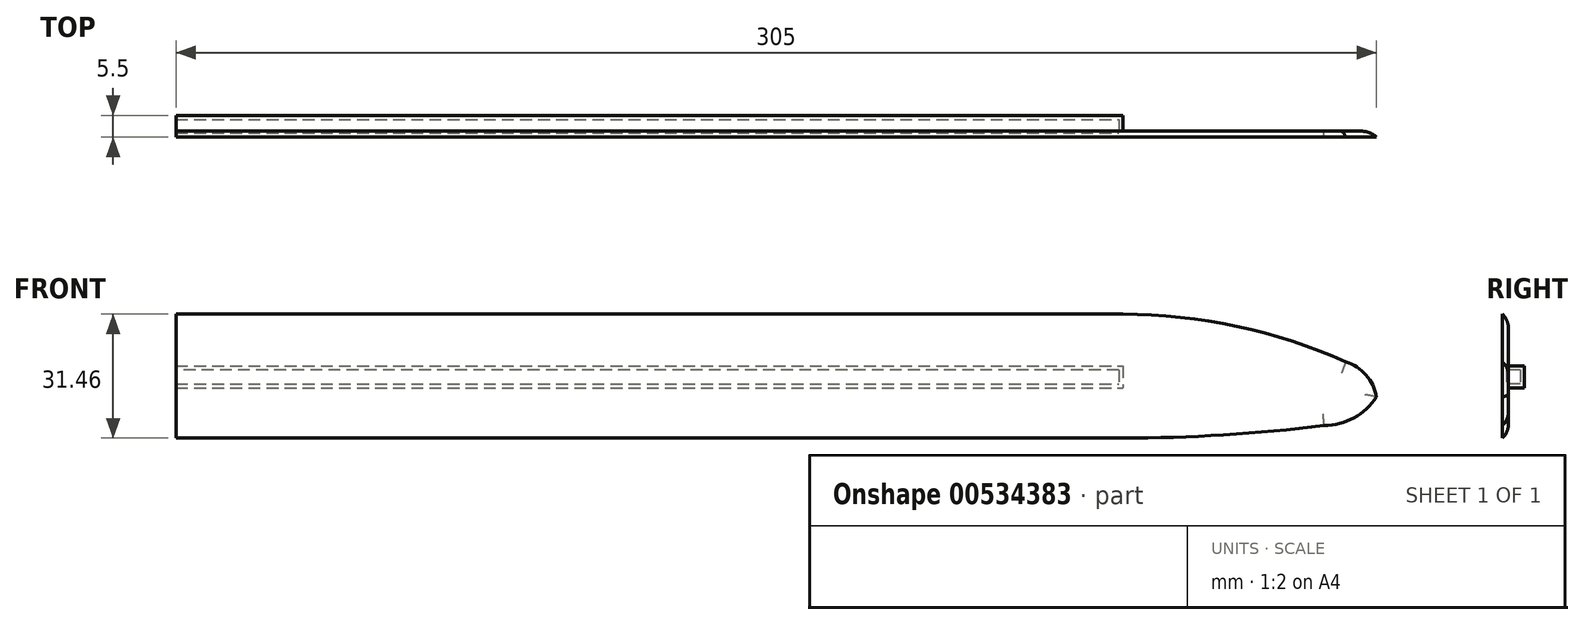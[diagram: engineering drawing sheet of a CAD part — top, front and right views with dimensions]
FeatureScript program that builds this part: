
annotation { "Feature Type Name" : "Feature", "Feature Type Description" : "" }
export const myFeature = defineFeature(function(context is Context, id is Id, definition is map)
    precondition{}
    {
        {
            var Q0;
            Q0=qCreatedBy(makeId("Front.planeOp"),FACE);
            var sketch = newSketch(context, id + "F0", { "sketchPlane" : qUnion([Q0])});
            skLineSegment(sketch, "E0.bottom", {"start": v(58.37, 30.14) * mm, "end": v(-182.18, 30.14) * mm});
            skLineSegment(sketch, "E0.top", {"start": v(58.37, -1.32) * mm, "end": v(-182.18, -1.32) * mm});
            skLineSegment(sketch, "E0.left", {"start": v(58.37, 30.14) * mm, "end": v(58.37, -1.32) * mm});
            skLineSegment(sketch, "E0.right", {"start": v(-182.18, 30.14) * mm, "end": v(-182.18, -1.32) * mm});
            skArc(sketch, "E1", {"start": v(114.98, 18.02) * mm, "mid": v(87.32, 27.07) * mm, "end": v(58.37, 30.14) * mm});
            skArc(sketch, "E2", {"start": v(58.37, -1.32) * mm, "mid": v(83.97, -0.52) * mm, "end": v(109.47, 1.86) * mm});
            skArc(sketch, "E3", {"start": v(109.47, 1.86) * mm, "mid": v(117.08, 3.8) * mm, "end": v(122.82, 9.16) * mm});
            skArc(sketch, "E4", {"start": v(122.82, 9.16) * mm, "mid": v(120.12, 14.67) * mm, "end": v(114.98, 18.02) * mm});
            skLineSegment(sketch, "E5.bottom", {"start": v(-182.18, 16.94) * mm, "end": v(58.37, 16.94) * mm});
            skLineSegment(sketch, "E5.top", {"start": v(-182.18, 11.36) * mm, "end": v(58.37, 11.36) * mm});
            skLineSegment(sketch, "E5.left", {"start": v(-182.18, 16.94) * mm, "end": v(-182.18, 11.36) * mm});
            skLineSegment(sketch, "E5.right", {"start": v(58.37, 16.94) * mm, "end": v(58.37, 11.36) * mm});
            skSolve(sketch);
        }
        {
            var Q0;
            {var subQ0=sQuery(id+"F0.wireOp",EDGE,"E0.bottom");Q0=makeQuery(id+"F0.imprint","IMPRINT",FACE,{"disambiguationData":[TD([[makeQuery(id+"F0.imprint","IMPRINT",EDGE,{"derivedFrom":subQ0}),1.0]])]});}
            var Q1;
            {var subQ0=sQuery(id+"F0.wireOp",EDGE,"E0.top");Q1=makeQuery(id+"F0.imprint","IMPRINT",FACE,{"disambiguationData":[TD([[makeQuery(id+"F0.imprint","IMPRINT",EDGE,{"derivedFrom":subQ0}),-1.0]])]});}
            var Q2;
            {var subQ0=sQuery(id+"F0.wireOp",EDGE,"E1");Q2=makeQuery(id+"F0.imprint","IMPRINT",FACE,{"disambiguationData":[TD([[makeQuery(id+"F0.imprint","IMPRINT",EDGE,{"derivedFrom":subQ0}),1.0]])]});}
            var Q3;
            Q3=makeQuery(id+"F0.imprint","IMPRINT",FACE,{"disambiguationData":[TD([[makeQuery(id+"F0.imprint","IMPRINT",EDGE,{"derivedFrom":sQuery(id+"F0.wireOp",EDGE,"E5.bottom")}),-1.0]])]});
            extrude(context, id + "F1", {"entities" : qUnion([Q0, Q1, Q2, Q3]), "depth" : 1.5 * mm, "offsetDistance" : 25 * mm});
        }
        {
            var Q0;
            Q0=makeQuery(id+"F0.imprint","IMPRINT",FACE,{"disambiguationData":[TD([[makeQuery(id+"F0.imprint","IMPRINT",EDGE,{"derivedFrom":sQuery(id+"F0.wireOp",EDGE,"E5.bottom")}),-1.0]])]});
            extrude(context, id + "F2", {"entities" : qUnion([Q0]), "operationType" : NewBodyOperationType.ADD, "oppositeDirection" : true, "depth" : 4 * mm, "offsetDistance" : 25 * mm});
        }
        {
            var Q0;
            Q0=makeQuery(id+"F2.opExtrude","CAP_EDGE",EDGE,{"disambiguationData":[OSD([sQuery(id+"F0.wireOp",EDGE,"E5.bottom")])],"isStart":true});
            var Q1;
            Q1=makeQuery(id+"F2.opExtrude","CAP_EDGE",EDGE,{"disambiguationData":[OSD([sQuery(id+"F0.wireOp",EDGE,"E5.top")])],"isStart":true});
            var Q2;
            Q2=makeQuery(id+"F1.opExtrude","CAP_EDGE",EDGE,{"disambiguationData":[OSD([sQuery(id+"F0.wireOp",EDGE,"E2")])],"isStart":true});
            var Q3;
            Q3=makeQuery(id+"F1.opExtrude","CAP_EDGE",EDGE,{"disambiguationData":[OSD([sQuery(id+"F0.wireOp",EDGE,"E3")])],"isStart":true});
            var Q4;
            Q4=makeQuery(id+"F1.opExtrude","CAP_EDGE",EDGE,{"disambiguationData":[OSD([sQuery(id+"F0.wireOp",EDGE,"E4")])],"isStart":true});
            var Q5;
            Q5=makeQuery(id+"F1.opExtrude","CAP_EDGE",EDGE,{"disambiguationData":[OSD([sQuery(id+"F0.wireOp",EDGE,"E1")])],"isStart":true});
            var Q6;
            Q6=makeQuery(id+"F2.opExtrude","CAP_EDGE",EDGE,{"disambiguationData":[OSD([sQuery(id+"F0.wireOp",EDGE,"E5.right")])],"isStart":true});
            fillet(context, id + "F3", {"entities" : qUnion([Q0, Q1, Q2, Q3, Q4, Q5, Q6]), "radius" : 5 * mm, "tangentPropagation" : true, "allowEdgeOverflow" : false});
        }
        {
            var Q0;
            {var subQ0=sQuery(id+"F0.wireOp",EDGE,"E5.left");Q0=makeQuery(id+"F2.boolean.opBoolean","MERGE",FACE,{"derivedFrom":[makeQuery(id+"F1.opExtrude","SWEPT_FACE",FACE,{"disambiguationData":[OSD([sQuery(id+"F0.wireOp",EDGE,"E0.right"),subQ0])]}),makeQuery(id+"F2.opExtrude","SWEPT_FACE",FACE,{"disambiguationData":[OSD([subQ0])]})]});}
            shell(context, id + "F4", {"entities" : qUnion([Q0]), "thickness" : 1 * mm});
        }
    });
